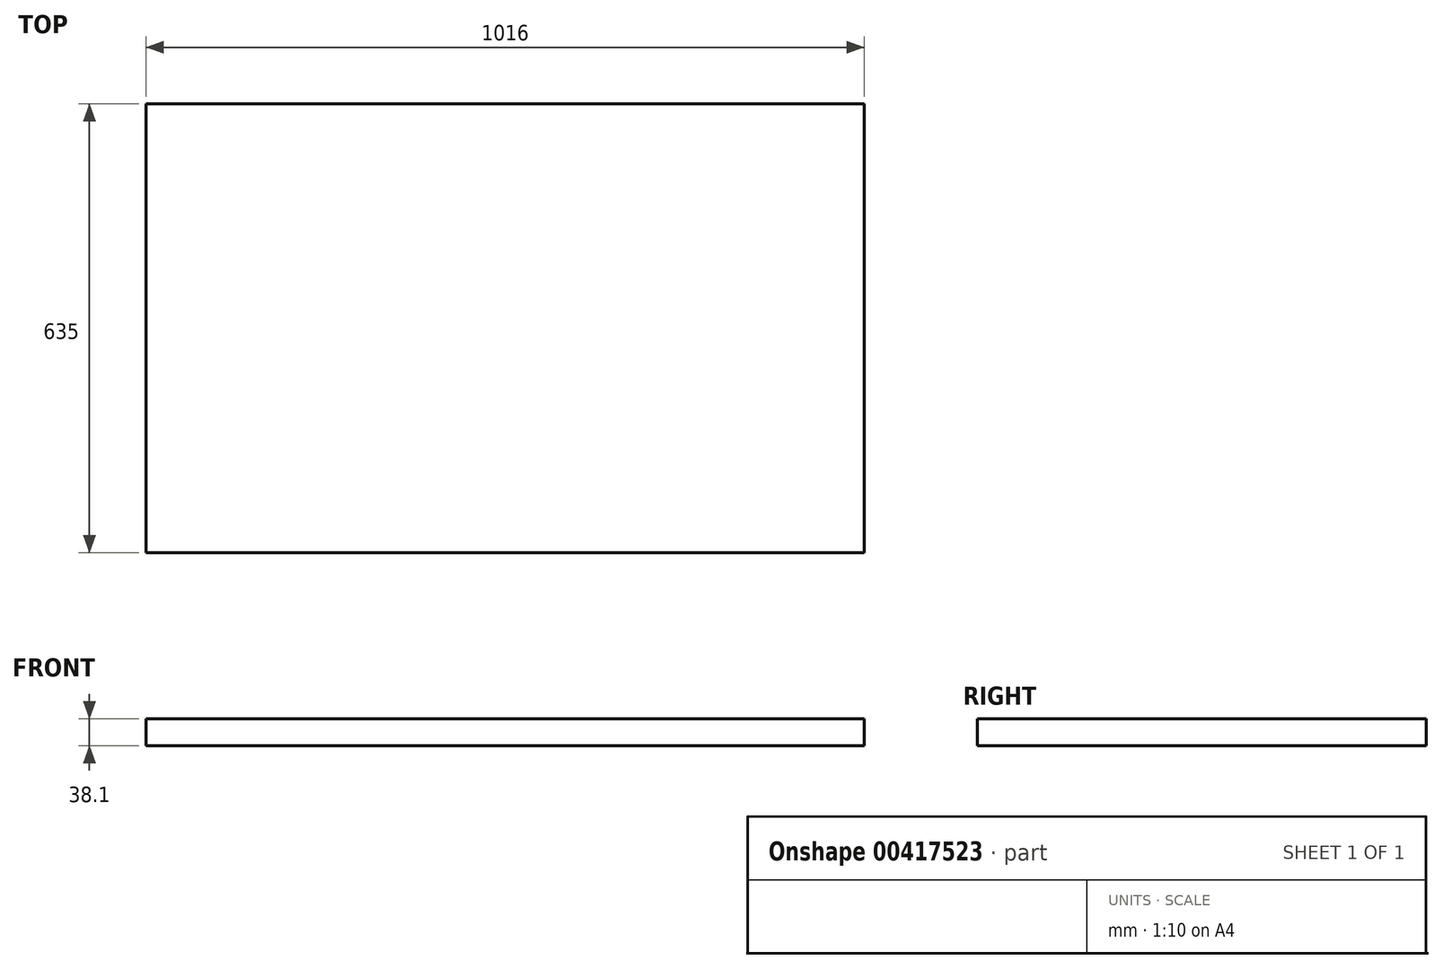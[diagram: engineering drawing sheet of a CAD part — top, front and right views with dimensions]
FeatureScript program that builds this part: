
annotation { "Feature Type Name" : "Feature", "Feature Type Description" : "" }
export const myFeature = defineFeature(function(context is Context, id is Id, definition is map)
    precondition{}
    {
        {
            var Q0;
            Q0=qCreatedBy(makeId("Top.planeOp"),FACE);
            var sketch = newSketch(context, id + "F0", { "sketchPlane" : qUnion([Q0])});
            skLineSegment(sketch, "E0.bottom", {"start": v(-504.73, 419.78) * mm, "end": v(511.27, 419.78) * mm});
            skLineSegment(sketch, "E0.top", {"start": v(-504.73, -215.22) * mm, "end": v(511.27, -215.22) * mm});
            skLineSegment(sketch, "E0.left", {"start": v(-504.73, 419.78) * mm, "end": v(-504.73, -215.22) * mm});
            skLineSegment(sketch, "E0.right", {"start": v(511.27, 419.78) * mm, "end": v(511.27, -215.22) * mm});
            skSolve(sketch);
        }
        {
            var Q0;
            Q0=makeQuery(id+"F0.imprint","IMPRINT",FACE,{"disambiguationData":[TD([[makeQuery(id+"F0.imprint","IMPRINT",EDGE,{"derivedFrom":sQuery(id+"F0.wireOp",EDGE,"E0.bottom")}),-1.0]])]});
            extrude(context, id + "F1", {"entities" : qUnion([Q0]), "oppositeDirection" : true, "depth" : 38.1 * mm});
        }
    });
